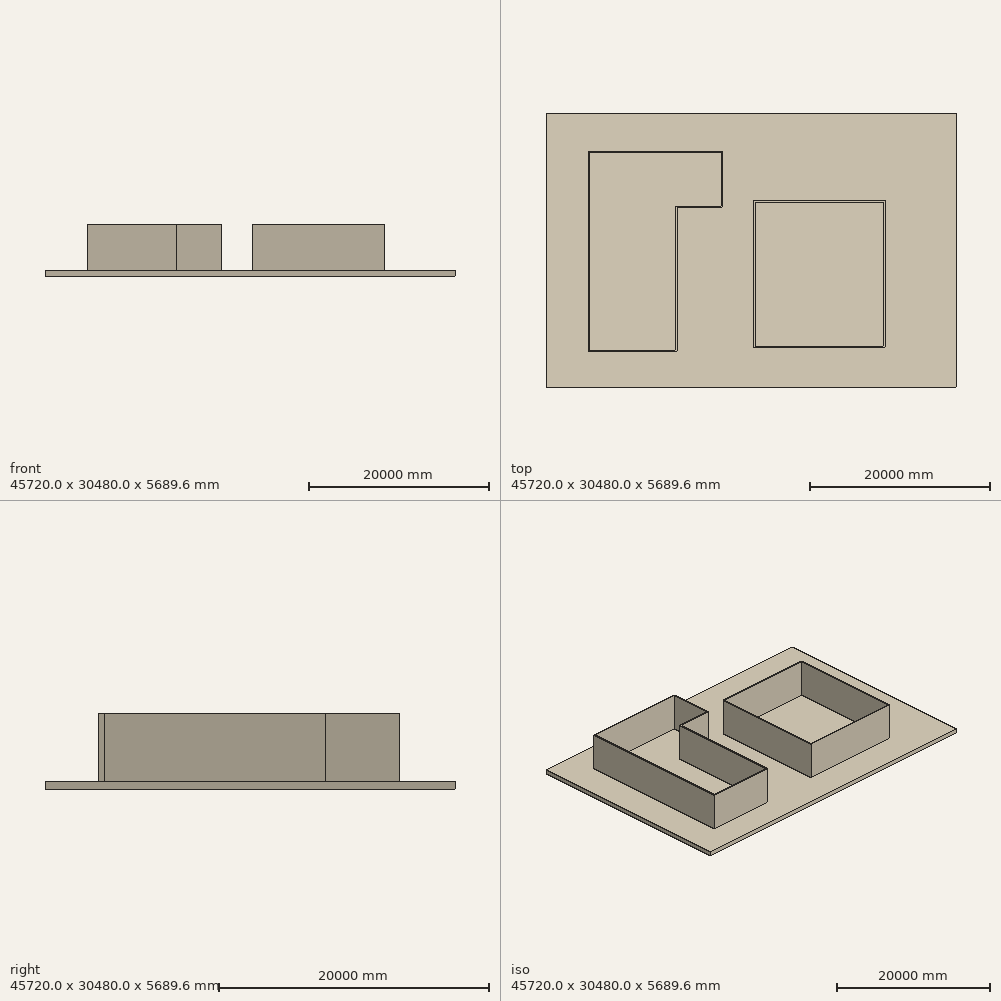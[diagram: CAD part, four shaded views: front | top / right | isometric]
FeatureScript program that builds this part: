
annotation { "Feature Type Name" : "Feature", "Feature Type Description" : "" }
export const myFeature = defineFeature(function(context is Context, id is Id, definition is map)
    precondition{}
    {
        {
            var Q0;
            Q0=qCreatedBy(makeId("Top.planeOp"),FACE);
            var sketch = newSketch(context, id + "F0", { "sketchPlane" : qUnion([Q0])});
            skLineSegment(sketch, "E0.rect.bottom", {"start": v(-22860, -15240) * mm, "end": v(22860, -15240) * mm});
            skLineSegment(sketch, "E0.rect.top", {"start": v(-22860, 15240) * mm, "end": v(22860, 15240) * mm});
            skLineSegment(sketch, "E0.rect.left", {"start": v(-22860, -15240) * mm, "end": v(-22860, 15240) * mm});
            skLineSegment(sketch, "E0.rect.right", {"start": v(22860, -15240) * mm, "end": v(22860, 15240) * mm});
            skPoint(sketch, "E0.rect.middle", {"position": v(0, 0) * mm});
            skSolve(sketch);
        }
        {
            var Q0;
            Q0 = qSketchRegion(id + "F0", true);
            extrude(context, id + "F1", {"entities" : qUnion([Q0]), "depth" : 609.6 * mm});
        }
        {
            var Q0;
            Q0=makeQuery(id+"F1.opExtrude","CAP_FACE",FACE,{"disambiguationData":[OSD([sQuery(id+"F0.wireOp",EDGE,"E0.rect.bottom"),sQuery(id+"F0.wireOp",EDGE,"E0.rect.top"),sQuery(id+"F0.wireOp",EDGE,"E0.rect.left"),sQuery(id+"F0.wireOp",EDGE,"E0.rect.right")])],"isStart":false});
            var sketch = newSketch(context, id + "F2", { "sketchPlane" : qUnion([Q0])});
            skLineSegment(sketch, "E1.bottom", {"start": v(13941.38, -15240) * mm, "end": v(1749.38, -15240) * mm});
            skLineSegment(sketch, "E1.top", {"start": v(13941.38, -10668) * mm, "end": v(1749.38, -10668) * mm});
            skLineSegment(sketch, "E1.left", {"start": v(13941.38, -15240) * mm, "end": v(13941.38, -10668) * mm});
            skLineSegment(sketch, "E1.right", {"start": v(1749.38, -15240) * mm, "end": v(1749.38, -10668) * mm});
            skLineSegment(sketch, "E2.bottom", {"start": v(420.33, -10668) * mm, "end": v(14740.5, -10668) * mm});
            skLineSegment(sketch, "E2.top", {"start": v(420.33, 5404.5) * mm, "end": v(14740.5, 5404.5) * mm});
            skLineSegment(sketch, "E2.left", {"start": v(420.33, -10668) * mm, "end": v(420.33, 5404.5) * mm});
            skLineSegment(sketch, "E2.right", {"start": v(14740.5, -10668) * mm, "end": v(14740.5, 5404.5) * mm});
            skLineSegment(sketch, "E3.top", {"start": v(-3385.68, 10939.4) * mm, "end": v(-18060.65, 10939.4) * mm});
            skLineSegment(sketch, "E3.left", {"start": v(-3385.68, 5400.04) * mm, "end": v(-3385.68, 10939.4) * mm});
            skLineSegment(sketch, "E3.right", {"start": v(-18060.65, 5400.04) * mm, "end": v(-18060.65, 10939.4) * mm});
            skLineSegment(sketch, "E4.top", {"start": v(-18060.65, -11154.26) * mm, "end": v(-8449.42, -11154.26) * mm});
            skLineSegment(sketch, "E4.left", {"start": v(-18060.65, 5400.04) * mm, "end": v(-18060.65, -11154.26) * mm});
            skLineSegment(sketch, "E5", {"start": v(-3385.68, 5400.04) * mm, "end": v(-3385.68, 4912.13) * mm});
            skLineSegment(sketch, "E6", {"start": v(-8449.42, -11154.26) * mm, "end": v(-8449.42, 4912.13) * mm});
            skLineSegment(sketch, "E7", {"start": v(-8449.42, 4912.13) * mm, "end": v(-3385.68, 4912.13) * mm});
            skLineSegment(sketch, "E8.0", {"start": v(-18213.05, -11306.66) * mm, "end": v(-8297.02, -11306.66) * mm});
            skLineSegment(sketch, "E8.1", {"start": v(-18213.05, 5400.04) * mm, "end": v(-18213.05, -11306.66) * mm});
            skLineSegment(sketch, "E8.2", {"start": v(-8297.02, -11306.66) * mm, "end": v(-8297.02, 4759.73) * mm});
            skLineSegment(sketch, "E8.3", {"start": v(-18213.05, 5400.04) * mm, "end": v(-18213.05, 11091.8) * mm});
            skLineSegment(sketch, "E8.4", {"start": v(-8297.02, 4759.73) * mm, "end": v(-3233.28, 4759.73) * mm});
            skLineSegment(sketch, "E8.5", {"start": v(-3233.28, 5400.04) * mm, "end": v(-3233.28, 4759.73) * mm});
            skLineSegment(sketch, "E8.6", {"start": v(-3233.28, 5400.04) * mm, "end": v(-3233.28, 11091.8) * mm});
            skLineSegment(sketch, "E8.7", {"start": v(-3233.28, 11091.8) * mm, "end": v(-18213.05, 11091.8) * mm});
            skLineSegment(sketch, "E9.0", {"start": v(267.93, -10820.4) * mm, "end": v(267.93, 5556.9) * mm});
            skLineSegment(sketch, "E9.1", {"start": v(267.93, -10820.4) * mm, "end": v(14892.9, -10820.4) * mm});
            skLineSegment(sketch, "E9.2", {"start": v(14892.9, -10820.4) * mm, "end": v(14892.9, 5556.9) * mm});
            skLineSegment(sketch, "E9.3", {"start": v(267.93, 5556.9) * mm, "end": v(14892.9, 5556.9) * mm});
            skSolve(sketch);
        }
        {
            var Q0;
            Q0=makeQuery(id+"F2.imprint","IMPRINT",FACE,{"disambiguationData":[TD([[makeQuery(id+"F2.imprint","IMPRINT",EDGE,{"derivedFrom":sQuery(id+"F2.wireOp",EDGE,"E3.top")}),-1.0]])]});
            var Q1;
            Q1=makeQuery(id+"F2.imprint","IMPRINT",FACE,{"disambiguationData":[TD([[makeQuery(id+"F2.imprint","IMPRINT",EDGE,{"derivedFrom":sQuery(id+"F2.wireOp",EDGE,"E2.top")}),1.0]])]});
            var Q2;
            {var subQ0=sQuery(id+"F2.wireOp",EDGE,"E2.bottom");var subQ1=sQuery(id+"F2.wireOp",EDGE,"E1.left");var subQ2=makeQuery(id+"F2.imprint","INTERSECT",VERTEX,{"derivedFrom":[subQ1,subQ0]});Q2=makeQuery(id+"F2.imprint","IMPRINT",FACE,{"disambiguationData":[TD([[makeQuery(id+"F2.imprint","IMPRINT",EDGE,{"disambiguationData":[TD([[subQ2,1.0]])],"derivedFrom":subQ1}),1.0]])]});}
            extrude(context, id + "F3", {"entities" : qUnion([Q0, Q1, Q2]), "depth" : 5080 * mm});
        }
    });
